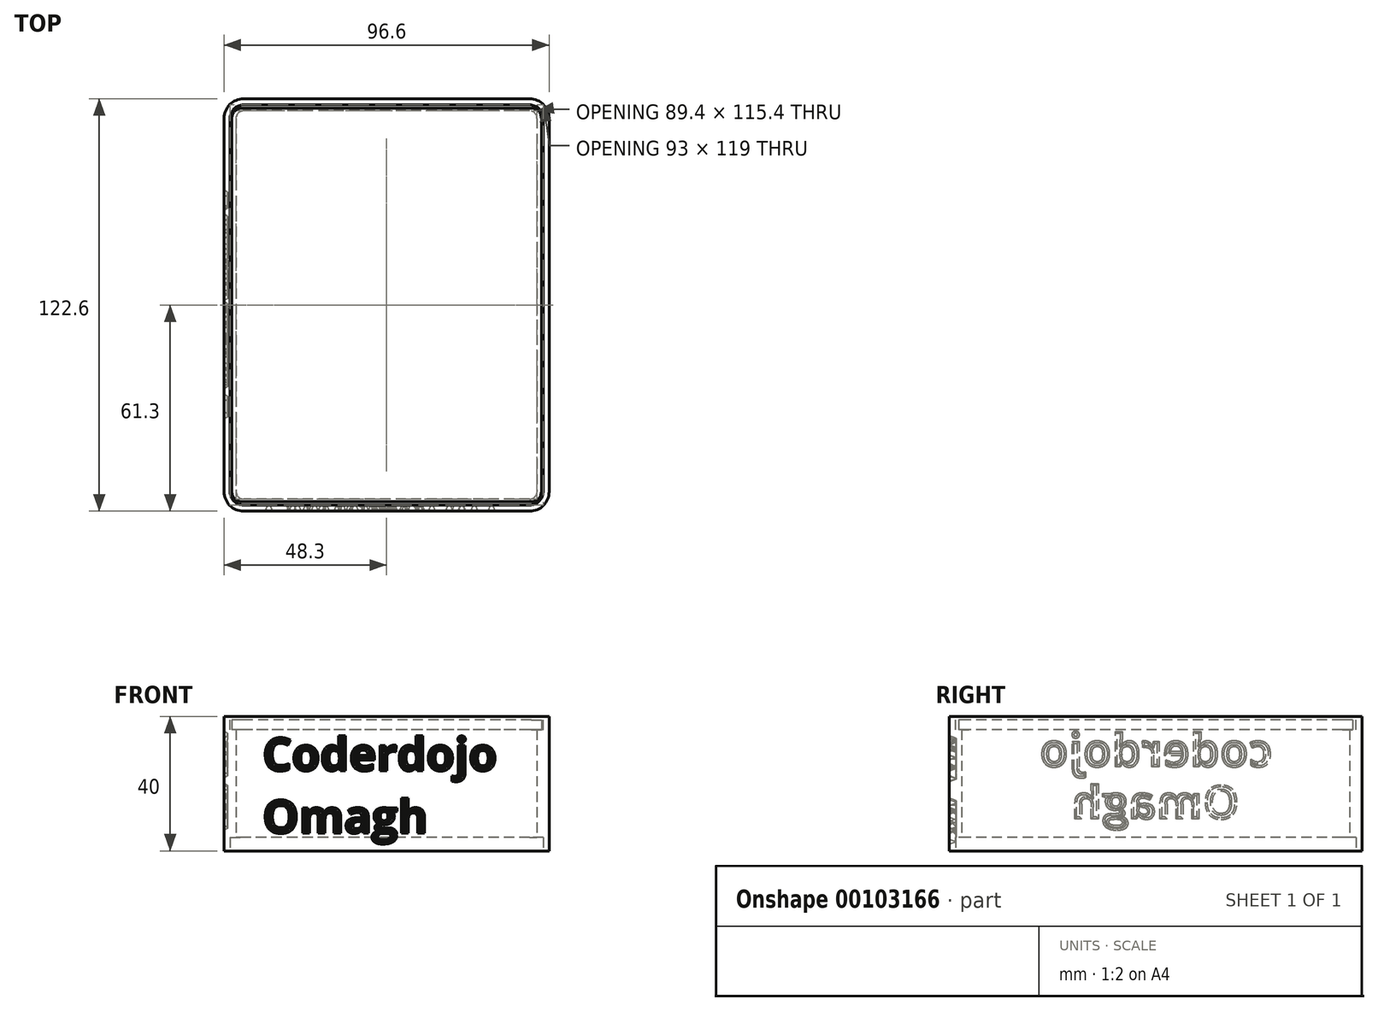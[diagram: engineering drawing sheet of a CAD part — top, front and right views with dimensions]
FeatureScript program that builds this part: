
annotation { "Feature Type Name" : "Feature", "Feature Type Description" : "" }
export const myFeature = defineFeature(function(context is Context, id is Id, definition is map)
    precondition{}
    {
        {
            var Q0;
            Q0=qCreatedBy(makeId("Top.planeOp"),FACE);
            var sketch = newSketch(context, id + "F0", { "sketchPlane" : qUnion([Q0])});
            skLineSegment(sketch, "E0.bottom", {"start": v(42.5, 59.5) * mm, "end": v(-42.5, 59.5) * mm});
            skLineSegment(sketch, "E0.top", {"start": v(42.5, -59.5) * mm, "end": v(-42.5, -59.5) * mm});
            skLineSegment(sketch, "E0.left", {"start": v(46.5, 55.5) * mm, "end": v(46.5, -55.5) * mm});
            skLineSegment(sketch, "E0.right", {"start": v(-46.5, 55.5) * mm, "end": v(-46.5, -55.5) * mm});
            skPoint(sketch, "E0.middle", {"position": v(0, 0) * mm});
            skPoint(sketch, "E1.visualSharp", {"position": v(-46.5, 59.5) * mm});
            skArc(sketch, "E1.filletArc", {"start": v(-42.5, 59.5) * mm, "mid": v(-45.33, 58.33) * mm, "end": v(-46.5, 55.5) * mm});
            skPoint(sketch, "E2.visualSharp", {"position": v(46.5, 59.5) * mm});
            skArc(sketch, "E2.filletArc", {"start": v(46.5, 55.5) * mm, "mid": v(45.33, 58.33) * mm, "end": v(42.5, 59.5) * mm});
            skPoint(sketch, "E3.visualSharp", {"position": v(46.5, -59.5) * mm});
            skArc(sketch, "E3.filletArc", {"start": v(42.5, -59.5) * mm, "mid": v(45.33, -58.33) * mm, "end": v(46.5, -55.5) * mm});
            skPoint(sketch, "E4.visualSharp", {"position": v(-46.5, -59.5) * mm});
            skArc(sketch, "E4.filletArc", {"start": v(-46.5, -55.5) * mm, "mid": v(-45.33, -58.33) * mm, "end": v(-42.5, -59.5) * mm});
            skArc(sketch, "E5.0", {"start": v(-42.5, 61.3) * mm, "mid": v(-46.6, 59.6) * mm, "end": v(-48.3, 55.5) * mm});
            skLineSegment(sketch, "E5.1", {"start": v(42.5, 61.3) * mm, "end": v(-42.5, 61.3) * mm});
            skLineSegment(sketch, "E5.2", {"start": v(-48.3, 55.5) * mm, "end": v(-48.3, -55.5) * mm});
            skArc(sketch, "E5.3", {"start": v(48.3, 55.5) * mm, "mid": v(46.6, 59.6) * mm, "end": v(42.5, 61.3) * mm});
            skArc(sketch, "E5.4", {"start": v(-48.3, -55.5) * mm, "mid": v(-46.6, -59.6) * mm, "end": v(-42.5, -61.3) * mm});
            skLineSegment(sketch, "E5.5", {"start": v(42.5, -61.3) * mm, "end": v(-42.5, -61.3) * mm});
            skArc(sketch, "E5.6", {"start": v(42.5, -61.3) * mm, "mid": v(46.6, -59.6) * mm, "end": v(48.3, -55.5) * mm});
            skLineSegment(sketch, "E5.7", {"start": v(48.3, 55.5) * mm, "end": v(48.3, -55.5) * mm});
            skArc(sketch, "E6.0", {"start": v(-42.5, 57.7) * mm, "mid": v(-44.06, 57.06) * mm, "end": v(-44.7, 55.5) * mm});
            skLineSegment(sketch, "E6.1", {"start": v(42.5, 57.7) * mm, "end": v(-42.5, 57.7) * mm});
            skLineSegment(sketch, "E6.2", {"start": v(-44.7, 55.5) * mm, "end": v(-44.7, -55.5) * mm});
            skArc(sketch, "E6.3", {"start": v(44.7, 55.5) * mm, "mid": v(44.06, 57.06) * mm, "end": v(42.5, 57.7) * mm});
            skArc(sketch, "E6.4", {"start": v(-44.7, -55.5) * mm, "mid": v(-44.06, -57.06) * mm, "end": v(-42.5, -57.7) * mm});
            skLineSegment(sketch, "E6.5", {"start": v(42.5, -57.7) * mm, "end": v(-42.5, -57.7) * mm});
            skArc(sketch, "E6.6", {"start": v(42.5, -57.7) * mm, "mid": v(44.06, -57.06) * mm, "end": v(44.7, -55.5) * mm});
            skLineSegment(sketch, "E6.7", {"start": v(44.7, 55.5) * mm, "end": v(44.7, -55.5) * mm});
            skSolve(sketch);
        }
        {
            var Q0;
            Q0=makeQuery(id+"F0.imprint","IMPRINT",FACE,{"disambiguationData":[TD([[makeQuery(id+"F0.imprint","IMPRINT",EDGE,{"derivedFrom":sQuery(id+"F0.wireOp",EDGE,"E0.bottom")}),-1.0]])]});
            var Q1;
            Q1=makeQuery(id+"F0.imprint","IMPRINT",FACE,{"disambiguationData":[TD([[makeQuery(id+"F0.imprint","IMPRINT",EDGE,{"derivedFrom":sQuery(id+"F0.wireOp",EDGE,"E0.bottom")}),1.0]])]});
            extrude(context, id + "F1", {"entities" : qUnion([Q0, Q1]), "depth" : 20 * mm});
        }
        {
            var Q0;
            Q0=makeQuery(id+"F0.imprint","IMPRINT",FACE,{"disambiguationData":[TD([[makeQuery(id+"F0.imprint","IMPRINT",EDGE,{"derivedFrom":sQuery(id+"F0.wireOp",EDGE,"E0.bottom")}),1.0]])]});
            extrude(context, id + "F2", {"entities" : qUnion([Q0]), "operationType" : NewBodyOperationType.REMOVE, "depth" : 4 * mm});
        }
        {
            var Q0;
            Q0=makeQuery(id+"F1.opExtrude","SWEPT_BODY",BODY,{"disambiguationData":[OSD([sQuery(id+"F0.wireOp",EDGE,"E5.0"),sQuery(id+"F0.wireOp",EDGE,"E5.1"),sQuery(id+"F0.wireOp",EDGE,"E5.2"),sQuery(id+"F0.wireOp",EDGE,"E5.3"),sQuery(id+"F0.wireOp",EDGE,"E5.4"),sQuery(id+"F0.wireOp",EDGE,"E5.5"),sQuery(id+"F0.wireOp",EDGE,"E5.6"),sQuery(id+"F0.wireOp",EDGE,"E5.7"),sQuery(id+"F0.wireOp",EDGE,"E6.0"),sQuery(id+"F0.wireOp",EDGE,"E6.1"),sQuery(id+"F0.wireOp",EDGE,"E6.2"),sQuery(id+"F0.wireOp",EDGE,"E6.3"),sQuery(id+"F0.wireOp",EDGE,"E6.4"),sQuery(id+"F0.wireOp",EDGE,"E6.5"),sQuery(id+"F0.wireOp",EDGE,"E6.6"),sQuery(id+"F0.wireOp",EDGE,"E6.7")])]});
            var Q1;
            Q1=makeQuery(id+"F1.opExtrude","CAP_FACE",FACE,{"disambiguationData":[OSD([sQuery(id+"F0.wireOp",EDGE,"E5.0"),sQuery(id+"F0.wireOp",EDGE,"E5.1"),sQuery(id+"F0.wireOp",EDGE,"E5.2"),sQuery(id+"F0.wireOp",EDGE,"E5.3"),sQuery(id+"F0.wireOp",EDGE,"E5.4"),sQuery(id+"F0.wireOp",EDGE,"E5.5"),sQuery(id+"F0.wireOp",EDGE,"E5.6"),sQuery(id+"F0.wireOp",EDGE,"E5.7"),sQuery(id+"F0.wireOp",EDGE,"E6.0"),sQuery(id+"F0.wireOp",EDGE,"E6.1"),sQuery(id+"F0.wireOp",EDGE,"E6.2"),sQuery(id+"F0.wireOp",EDGE,"E6.3"),sQuery(id+"F0.wireOp",EDGE,"E6.4"),sQuery(id+"F0.wireOp",EDGE,"E6.5"),sQuery(id+"F0.wireOp",EDGE,"E6.6"),sQuery(id+"F0.wireOp",EDGE,"E6.7")])],"isStart":false});
            mirror(context, id + "F3", {"operationType" : NewBodyOperationType.ADD, "entities" : qUnion([Q0]), "mirrorPlane" : qUnion([Q1])});
        }
        {
            var Q0;
            {var subQ0=makeQuery(id+"F1.opExtrude","SWEPT_FACE",FACE,{"disambiguationData":[OSD([sQuery(id+"F0.wireOp",EDGE,"E5.2")])]});Q0=makeQuery(id+"F3.boolean.opBoolean","MERGE",FACE,{"derivedFrom":[subQ0,makeQuery(id+"F3.opPattern","COPY",FACE,{"derivedFrom":subQ0,"instanceName":"1"})]});}
            var sketch = newSketch(context, id + "F4", { "sketchPlane" : qUnion([Q0])});
            skText(sketch, "E7", { "text": "coderdojo", "fontName": "OpenSans-Bold.ttf"});
            skText(sketch, "E8", { "text": "Omagh", "fontName": "OpenSans-Bold.ttf"});
            const initialGuessF4  = {"E7": [-0.03477, 0.025, 1, 0, 0.01], "E8": [-0.02496, 0.0095, 1, 0, 0.01]};
            skSetInitialGuess(sketch, initialGuessF4);
            skSolve(sketch);
        }
        {
            var Q0;
            {var subQ0=makeQuery(id+"F1.opExtrude","SWEPT_FACE",FACE,{"disambiguationData":[OSD([sQuery(id+"F0.wireOp",EDGE,"E5.5")])]});Q0=makeQuery(id+"F3.boolean.opBoolean","MERGE",FACE,{"derivedFrom":[subQ0,makeQuery(id+"F3.opPattern","COPY",FACE,{"derivedFrom":subQ0,"instanceName":"1"})]});}
            var sketch = newSketch(context, id + "F5", { "sketchPlane" : qUnion([Q0])});
            skText(sketch, "E9", { "text": "Coderdojo\nOmagh", "fontName": "OpenSans-Bold.ttf"});
            const initialGuessF5  = {"E9": [-0.03688, 0.02384, 1, 0, 0.00982]};
            skSetInitialGuess(sketch, initialGuessF5);
            skSolve(sketch);
        }
        {
            var Q0;
            Q0 = qSketchRegion(id + "F5", true);
            extrude(context, id + "F6", {"entities" : qUnion([Q0]), "operationType" : NewBodyOperationType.REMOVE, "oppositeDirection" : true, "depth" : 2 * mm, "hasDraft" : true, "draftAngle" : 20 * degree, "draftPullDirection" : true});
        }
        {
            var Q0;
            Q0=makeQuery(id+"F3.opPattern","COPY",FACE,{"derivedFrom":makeQuery(id+"F2.boolean.opBoolean","COPY",FACE,{"derivedFrom":makeQuery(id+"F2.opExtrude","CAP_FACE",FACE,{"disambiguationData":[OSD([sQuery(id+"F0.wireOp",EDGE,"E0.bottom"),sQuery(id+"F0.wireOp",EDGE,"E0.top"),sQuery(id+"F0.wireOp",EDGE,"E0.left"),sQuery(id+"F0.wireOp",EDGE,"E0.right"),sQuery(id+"F0.wireOp",EDGE,"E1.filletArc"),sQuery(id+"F0.wireOp",EDGE,"E2.filletArc"),sQuery(id+"F0.wireOp",EDGE,"E3.filletArc"),sQuery(id+"F0.wireOp",EDGE,"E4.filletArc"),sQuery(id+"F0.wireOp",EDGE,"E6.0"),sQuery(id+"F0.wireOp",EDGE,"E6.1"),sQuery(id+"F0.wireOp",EDGE,"E6.2"),sQuery(id+"F0.wireOp",EDGE,"E6.3"),sQuery(id+"F0.wireOp",EDGE,"E6.4"),sQuery(id+"F0.wireOp",EDGE,"E6.5"),sQuery(id+"F0.wireOp",EDGE,"E6.6"),sQuery(id+"F0.wireOp",EDGE,"E6.7")])],"isStart":false})}),"instanceName":"1"});
            var sketch = newSketch(context, id + "F7", { "sketchPlane" : qUnion([Q0])});
            skLineSegment(sketch, "E10.bottom", {"start": v(43, 58.5) * mm, "end": v(-43, 58.5) * mm});
            skLineSegment(sketch, "E10.top", {"start": v(43, -58.5) * mm, "end": v(-43, -58.5) * mm});
            skLineSegment(sketch, "E10.left", {"start": v(46, 55.5) * mm, "end": v(46, -55.5) * mm});
            skLineSegment(sketch, "E10.right", {"start": v(-46, 55.5) * mm, "end": v(-46, -55.5) * mm});
            skPoint(sketch, "E10.middle", {"position": v(0, 0) * mm});
            skPoint(sketch, "E11.visualSharp", {"position": v(-46, 58.5) * mm});
            skArc(sketch, "E11.filletArc", {"start": v(-43, 58.5) * mm, "mid": v(-45.12, 57.62) * mm, "end": v(-46, 55.5) * mm});
            skPoint(sketch, "E12.visualSharp", {"position": v(46, 58.5) * mm});
            skArc(sketch, "E12.filletArc", {"start": v(46, 55.5) * mm, "mid": v(45.12, 57.62) * mm, "end": v(43, 58.5) * mm});
            skPoint(sketch, "E13.visualSharp", {"position": v(-46, -58.5) * mm});
            skArc(sketch, "E13.filletArc", {"start": v(-46, -55.5) * mm, "mid": v(-45.12, -57.62) * mm, "end": v(-43, -58.5) * mm});
            skPoint(sketch, "E14.visualSharp", {"position": v(46, -58.5) * mm});
            skArc(sketch, "E14.filletArc", {"start": v(43, -58.5) * mm, "mid": v(45.12, -57.62) * mm, "end": v(46, -55.5) * mm});
            skSolve(sketch);
        }
        {
            var Q0;
            Q0 = qSketchRegion(id + "F7", true);
            extrude(context, id + "F8", {"entities" : qUnion([Q0]), "depth" : 3 * mm});
        }
        {
            var Q0;
            Q0 = qSketchRegion(id + "F4", true);
            extrude(context, id + "F9", {"entities" : qUnion([Q0]), "operationType" : NewBodyOperationType.REMOVE, "oppositeDirection" : true, "depth" : 1 * mm, "hasDraft" : true, "draftAngle" : 30 * degree, "draftPullDirection" : true});
        }
    });
